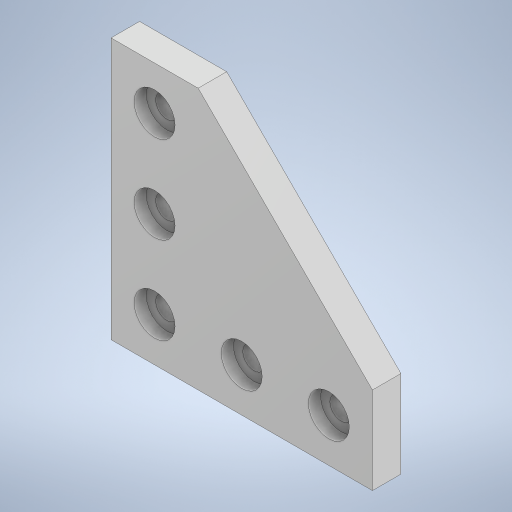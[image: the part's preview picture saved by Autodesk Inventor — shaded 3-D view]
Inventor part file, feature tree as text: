
AUTODESK INVENTOR PART (.ipt)
format: ipt  version: 2024 (Build 280153000, 153)  size: 290,816 bytes
history: native  units: in
note: dims shown in document units (in); Inventor stores cm internally (conversion verified against a paired STEP export)
features: extrude x1, sketch x1, other x1
ambient origin geometry x8: Origin, YZ Plane, XZ Plane, XY Plane, X Axis, Y Axis, Z Axis, Center Point
bodies: Solid1 (feature_tree)
feature tree (3):
  extrude  "Extrusion1"  Depth=0.14in
  sketch  "Sketch1"  dims[d0=0.47in d1=0.47in d2=0.47in d3=0.47in d4=0.47in d5=0.14in d6=0.0in]
  other  "Boss-Extrude1"
